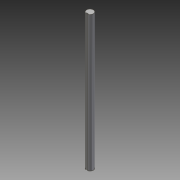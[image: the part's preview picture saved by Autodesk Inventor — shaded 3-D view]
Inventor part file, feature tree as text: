
AUTODESK INVENTOR PART (.ipt)
format: ipt  version: 2014 SP1 (Build 180222100, 222)  size: 72,192 bytes
history: native  units: in
note: dims shown in document units (in); Inventor stores cm internally (conversion verified against a paired STEP export)
features: extrude x1, sketch x1
ambient origin geometry x8: Origin, YZ Plane, XZ Plane, XY Plane, X Axis, Y Axis, Z Axis, Center Point
bodies: Solid1 (feature_tree)
feature tree (2):
  extrude  "Extrusion1"  Depth=0.0787in
  sketch  "Sketch1"  dims[d0=0.315in d1=0.0787in d2=0.0394in d3=0.0394in d4=6.25in d5=0.0in]
